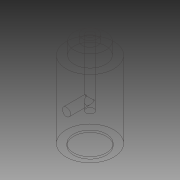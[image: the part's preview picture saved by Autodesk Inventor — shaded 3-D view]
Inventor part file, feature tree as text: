
AUTODESK INVENTOR PART (.ipt)
format: ipt  version: 2012 SP1 (Build 160190100, 190)  size: 118,784 bytes
history: native  units: in
note: dims shown in document units (in); Inventor stores cm internally (conversion verified against a paired STEP export)
features: sketch x2, revolve x1, plane x1, hole x1
ambient origin geometry x8: Origin, YZ Plane, XZ Plane, XY Plane, X Axis, Y Axis, Z Axis, Center Point
bodies: Solid1 (feature_tree)
feature tree (5):
  revolve  "Revolution1"  [1 undecoded]
  plane  "Work Plane1"
  hole  "Hole2"  [1 undecoded]
  sketch  "Sketch1"  dims[d0=0.2333in d1=0.1555in]
  sketch  "Sketch7"  dims[d2=0.039in d3=0.1604in d4=0.02in d5=0.9476in d7=0.89in d10=90.0deg d16=0.65in d21=0.076in d33=0.08in d34=0.125in d35=0.375in d36=0.25in d37=0.5635in d38=0.233in d39=0.0in d40=0.75in d41=0.385in d24=0.0394in d25=0.0394in]
note: 2 required parameter values undecoded (feature->parameter linkage not recoverable at this tier; creation-order binding heuristic only, values carry confidence <= 0.55)